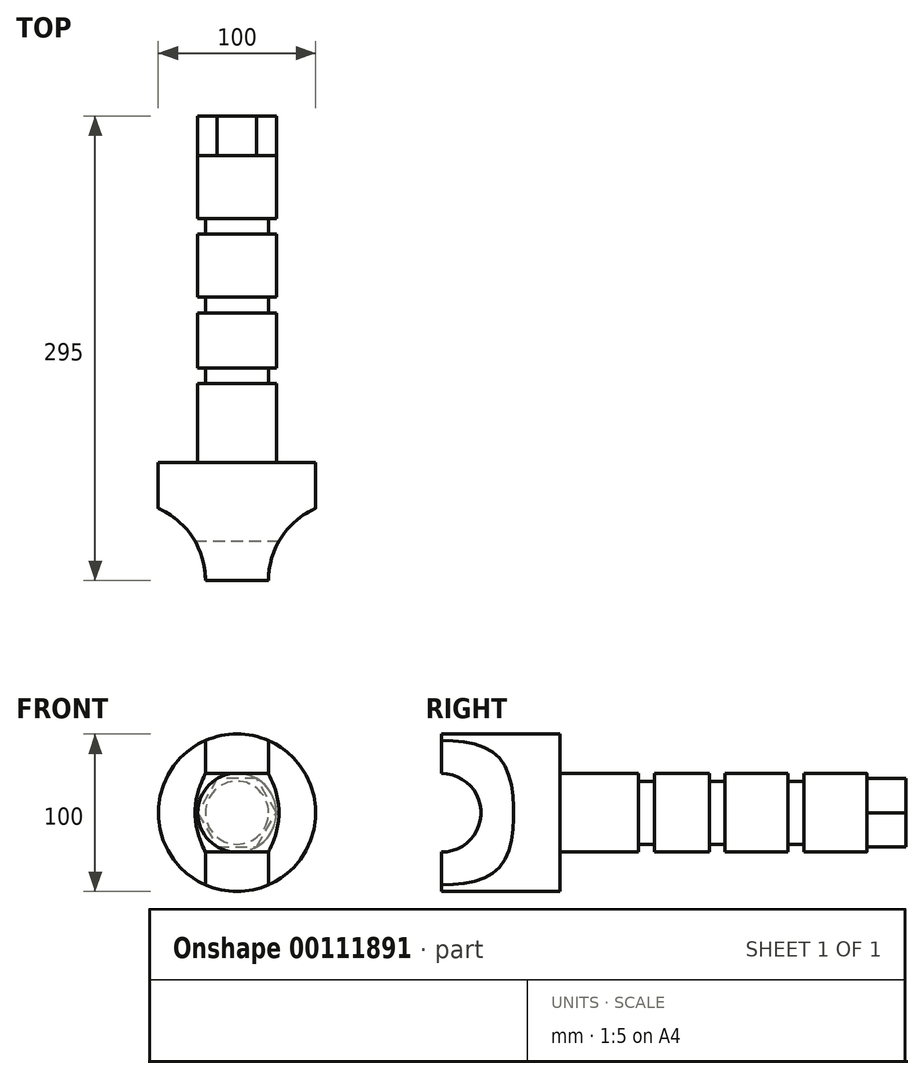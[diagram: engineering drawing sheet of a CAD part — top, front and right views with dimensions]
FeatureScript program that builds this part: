
annotation { "Feature Type Name" : "Feature", "Feature Type Description" : "" }
export const myFeature = defineFeature(function(context is Context, id is Id, definition is map)
    precondition{}
    {
        {
            var Q0;
            Q0=qCreatedBy(makeId("Front.planeOp"),FACE);
            var sketch = newSketch(context, id + "F0", { "sketchPlane" : qUnion([Q0])});
            skCircle(sketch, "E0", {"center": v(0, 0) * mm, "radius": 50 * mm});
            skSolve(sketch);
        }
        {
            var Q0;
            Q0 = qSketchRegion(id + "F0", true);
            extrude(context, id + "F1", {"entities" : qUnion([Q0]), "depth" : 75 * mm});
        }
        {
            var Q0;
            Q0=makeQuery(id+"F1.opExtrude","CAP_FACE",FACE,{"disambiguationData":[OSD([sQuery(id+"F0.wireOp",EDGE,"E0")])],"isStart":true});
            var sketch = newSketch(context, id + "F2", { "sketchPlane" : qUnion([Q0])});
            skCircle(sketch, "E1", {"center": v(0, 0) * mm, "radius": 25 * mm});
            skSolve(sketch);
        }
        {
            var Q0;
            Q0 = qSketchRegion(id + "F2", true);
            extrude(context, id + "F3", {"entities" : qUnion([Q0]), "operationType" : NewBodyOperationType.ADD, "depth" : 50 * mm});
        }
        {
            var Q0;
            Q0=makeQuery(id+"F3.opExtrude","CAP_FACE",FACE,{"disambiguationData":[OSD([sQuery(id+"F2.wireOp",EDGE,"E1")])],"isStart":false});
            var sketch = newSketch(context, id + "F4", { "sketchPlane" : qUnion([Q0])});
            skCircle(sketch, "E2", {"center": v(0, 0) * mm, "radius": 20 * mm});
            skSolve(sketch);
        }
        {
            var Q0;
            Q0 = qSketchRegion(id + "F4", true);
            extrude(context, id + "F5", {"entities" : qUnion([Q0]), "operationType" : NewBodyOperationType.ADD, "depth" : 10 * mm});
        }
        {
            var Q0;
            Q0=makeQuery(id+"F5.opExtrude","CAP_FACE",FACE,{"disambiguationData":[OSD([sQuery(id+"F4.wireOp",EDGE,"E2")])],"isStart":false});
            var sketch = newSketch(context, id + "F6", { "sketchPlane" : qUnion([Q0])});
            skCircle(sketch, "E3", {"center": v(0, 0) * mm, "radius": 25 * mm});
            skSolve(sketch);
        }
        {
            var Q0;
            Q0 = qSketchRegion(id + "F6", true);
            extrude(context, id + "F7", {"entities" : qUnion([Q0]), "operationType" : NewBodyOperationType.ADD, "depth" : 35 * mm});
        }
        {
            var Q0;
            Q0=makeQuery(id+"F7.opExtrude","CAP_FACE",FACE,{"disambiguationData":[OSD([sQuery(id+"F6.wireOp",EDGE,"E3")])],"isStart":false});
            var sketch = newSketch(context, id + "F8", { "sketchPlane" : qUnion([Q0])});
            skCircle(sketch, "E4", {"center": v(0, 0) * mm, "radius": 20 * mm});
            skSolve(sketch);
        }
        {
            var Q0;
            Q0 = qSketchRegion(id + "F8", true);
            extrude(context, id + "F9", {"entities" : qUnion([Q0]), "operationType" : NewBodyOperationType.ADD, "depth" : 10 * mm});
        }
        {
            var Q0;
            Q0=makeQuery(id+"F9.opExtrude","CAP_FACE",FACE,{"disambiguationData":[OSD([sQuery(id+"F8.wireOp",EDGE,"E4")])],"isStart":false});
            var sketch = newSketch(context, id + "F10", { "sketchPlane" : qUnion([Q0])});
            skCircle(sketch, "E5", {"center": v(0, 0) * mm, "radius": 25 * mm});
            skSolve(sketch);
        }
        {
            var Q0;
            Q0 = qSketchRegion(id + "F10", true);
            extrude(context, id + "F11", {"entities" : qUnion([Q0]), "operationType" : NewBodyOperationType.ADD, "depth" : 40 * mm});
        }
        {
            var Q0;
            Q0=makeQuery(id+"F11.opExtrude","CAP_FACE",FACE,{"disambiguationData":[OSD([sQuery(id+"F10.wireOp",EDGE,"E5")])],"isStart":false});
            var sketch = newSketch(context, id + "F12", { "sketchPlane" : qUnion([Q0])});
            skCircle(sketch, "E6", {"center": v(0, 0) * mm, "radius": 20 * mm});
            skSolve(sketch);
        }
        {
            var Q0;
            Q0 = qSketchRegion(id + "F12", true);
            extrude(context, id + "F13", {"entities" : qUnion([Q0]), "operationType" : NewBodyOperationType.ADD, "depth" : 10 * mm});
        }
        {
            var Q0;
            Q0=makeQuery(id+"F13.opExtrude","CAP_FACE",FACE,{"disambiguationData":[OSD([sQuery(id+"F12.wireOp",EDGE,"E6")])],"isStart":false});
            var sketch = newSketch(context, id + "F14", { "sketchPlane" : qUnion([Q0])});
            skCircle(sketch, "E7", {"center": v(0, 0) * mm, "radius": 25 * mm});
            skSolve(sketch);
        }
        {
            var Q0;
            Q0 = qSketchRegion(id + "F14", true);
            extrude(context, id + "F15", {"entities" : qUnion([Q0]), "operationType" : NewBodyOperationType.ADD, "depth" : 40 * mm});
        }
        {
            var Q0;
            Q0=makeQuery(id+"F15.opExtrude","CAP_FACE",FACE,{"disambiguationData":[OSD([sQuery(id+"F14.wireOp",EDGE,"E7")])],"isStart":false});
            var sketch = newSketch(context, id + "F16", { "sketchPlane" : qUnion([Q0])});
            skCircle(sketch, "E8.cCircle", {"center": v(0, 0) * mm, "radius": 21.65 * mm, "construction": true});
            skLineSegment(sketch, "E8.0", {"start": v(-12.5, 21.65) * mm, "end": v(12.5, 21.65) * mm});
            skLineSegment(sketch, "E8.1", {"start": v(12.5, 21.65) * mm, "end": v(25, 0) * mm});
            skLineSegment(sketch, "E8.2", {"start": v(25, 0) * mm, "end": v(12.5, -21.65) * mm});
            skLineSegment(sketch, "E8.3", {"start": v(12.5, -21.65) * mm, "end": v(-12.5, -21.65) * mm});
            skLineSegment(sketch, "E8.4", {"start": v(-12.5, -21.65) * mm, "end": v(-25, 0) * mm});
            skLineSegment(sketch, "E8.5", {"start": v(-25, 0) * mm, "end": v(-12.5, 21.65) * mm});
            skPoint(sketch, "E8.0.midPoint", {"position": v(0, 21.65) * mm});
            skSolve(sketch);
        }
        {
            var Q0;
            Q0 = qSketchRegion(id + "F16", true);
            extrude(context, id + "F17", {"entities" : qUnion([Q0]), "operationType" : NewBodyOperationType.ADD, "depth" : 25 * mm});
        }
        {
            var Q0;
            Q0=makeQuery(id+"F1.opExtrude","CAP_FACE",FACE,{"disambiguationData":[OSD([sQuery(id+"F0.wireOp",EDGE,"E0")])],"isStart":false});
            var sketch = newSketch(context, id + "F18", { "sketchPlane" : qUnion([Q0])});
            skLineSegment(sketch, "E9", {"start": v(20, 45.83) * mm, "end": v(20, -45.83) * mm});
            skPoint(sketch, "E10", {"position": v(20, 45.83) * mm});
            skPoint(sketch, "E11", {"position": v(20, -45.83) * mm});
            skArc(sketch, "E12", {"start": v(20, -45.83) * mm, "mid": v(50, 0) * mm, "end": v(20, 45.83) * mm});
            skLineSegment(sketch, "E13", {"start": v(70, 23.5) * mm, "end": v(70, -24.63) * mm, "construction": true});
            skSolve(sketch);
        }
        {
            var Q0;
            Q0=makeQuery(id+"F18.imprint","IMPRINT",FACE,{"disambiguationData":[TD([[makeQuery(id+"F18.imprint","IMPRINT",EDGE,{"derivedFrom":sQuery(id+"F18.wireOp",EDGE,"E9")}),1.0]])]});
            var Q1;
            Q1=makeQuery(id+"F18.imprint","IMPRINT",FACE,{"disambiguationData":[TD([[makeQuery(id+"F18.imprint","IMPRINT",EDGE,{"derivedFrom":sQuery(id+"F18.wireOp",EDGE,"99bf100b-b2cd-47d8-92b8-f6f7eee58e6f0.MirrorCS")}),-1.0]])]});
            var Q2;
            Q2=sQuery(id+"F18.wireOp",EDGE,"E9");
            var Q3;
            Q3=sQuery(id+"F18.wireOp",EDGE,"E12");
            var Q4;
            Q4=sQuery(id+"F18.wireOp",EDGE,"E13");
            revolve(context, id + "F19", {"operationType" : NewBodyOperationType.REMOVE, "entities" : qUnion([Q0, Q1]), "surfaceEntities" : qUnion([Q2, Q3]), "axis" : qUnion([Q4]), "revolveType" : RevolveType.ONE_DIRECTION, "angle" : 90 * degree});
        }
        {
            var Q0;
            Q0=makeQuery(id+"F1.opExtrude","CAP_FACE",FACE,{"disambiguationData":[OSD([sQuery(id+"F0.wireOp",EDGE,"E0")])],"isStart":false});
            var sketch = newSketch(context, id + "F20", { "sketchPlane" : qUnion([Q0])});
            skLineSegment(sketch, "E14", {"start": v(-20, 45.83) * mm, "end": v(-20, -45.83) * mm});
            skArc(sketch, "E15", {"start": v(-20, 45.83) * mm, "mid": v(-50, 0) * mm, "end": v(-20, -45.83) * mm});
            skLineSegment(sketch, "E16", {"start": v(-70, 22.91) * mm, "end": v(-70, -24.27) * mm, "construction": true});
            skSolve(sketch);
        }
        {
            var Q0;
            Q0 = qSketchRegion(id + "F20", true);
            var Q1;
            Q1=sQuery(id+"F20.wireOp",EDGE,"E16");
            revolve(context, id + "F21", {"operationType" : NewBodyOperationType.REMOVE, "entities" : qUnion([Q0]), "axis" : qUnion([Q1]), "revolveType" : RevolveType.FULL, "oppositeDirection" : true});
        }
        {
            var Q0;
            Q0=qCreatedBy(makeId("Right.planeOp"),FACE);
            var sketch = newSketch(context, id + "F22", { "sketchPlane" : qUnion([Q0])});
            skCircle(sketch, "E17", {"center": v(-75, 0) * mm, "radius": 25 * mm});
            skSolve(sketch);
        }
        {
            var Q0;
            Q0 = qSketchRegion(id + "F22", true);
            extrude(context, id + "F23", {"entities" : qUnion([Q0]), "operationType" : NewBodyOperationType.REMOVE, "endBound" : BoundingType.SYMMETRIC, "oppositeDirection" : true, "depth" : 100 * mm});
        }
    });
